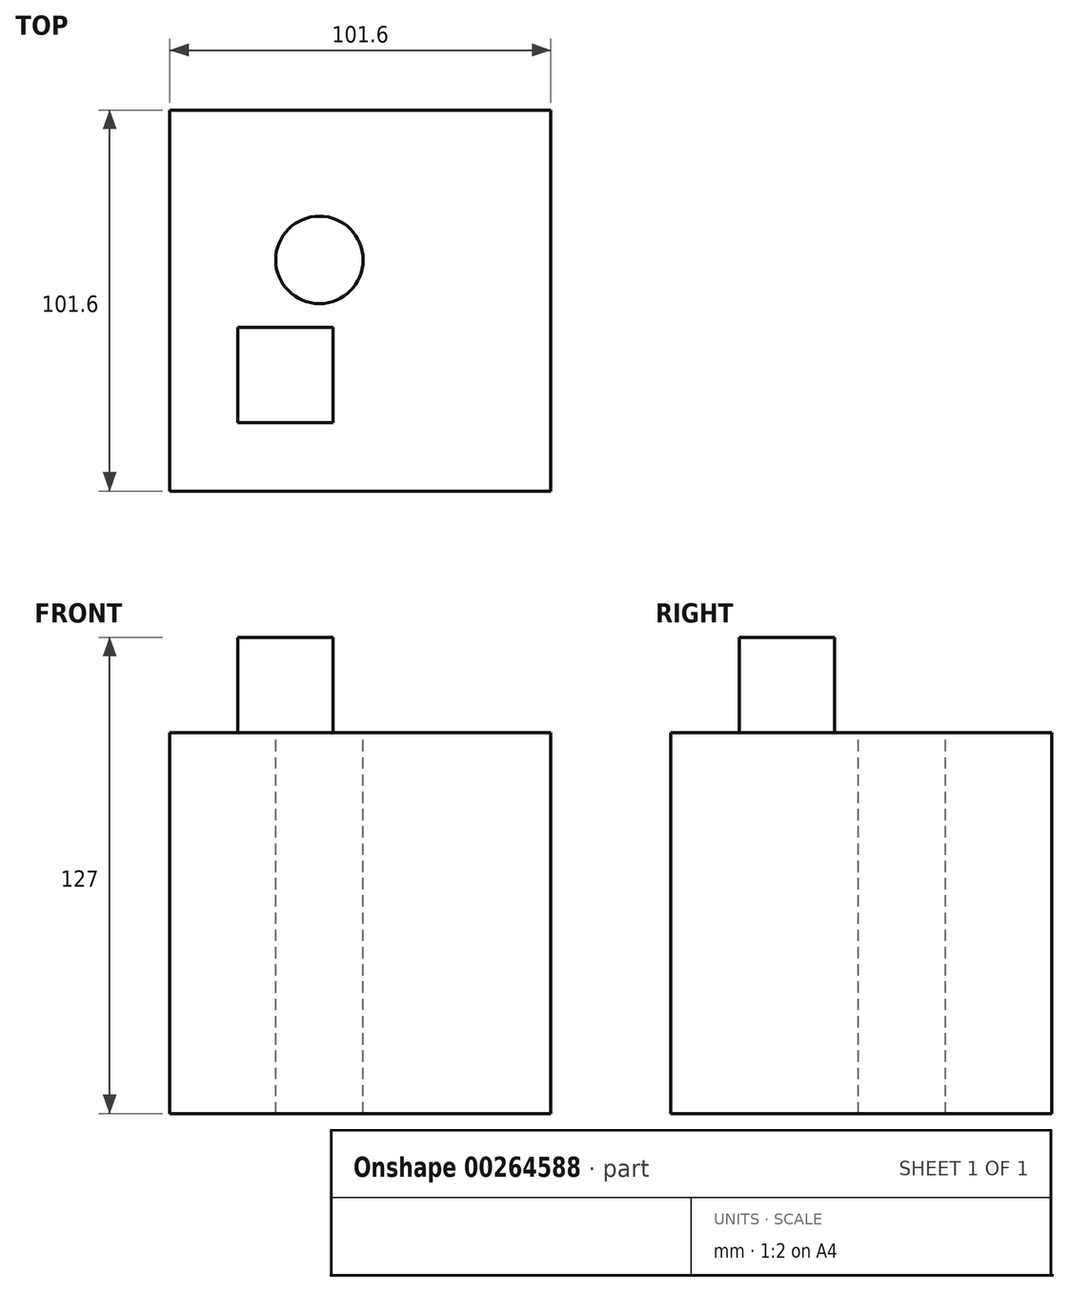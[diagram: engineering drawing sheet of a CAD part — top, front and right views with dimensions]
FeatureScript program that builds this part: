
annotation { "Feature Type Name" : "Feature", "Feature Type Description" : "" }
export const myFeature = defineFeature(function(context is Context, id is Id, definition is map)
    precondition{}
    {
        {
            var Q0;
            Q0=qCreatedBy(makeId("Front.planeOp"),FACE);
            var sketch = newSketch(context, id + "F0", { "sketchPlane" : qUnion([Q0])});
            skLineSegment(sketch, "E0.bottom", {"start": v(0, 0) * mm, "end": v(-101.6, 0) * mm});
            skLineSegment(sketch, "E0.top", {"start": v(0, 101.6) * mm, "end": v(-101.6, 101.6) * mm});
            skLineSegment(sketch, "E0.left", {"start": v(0, 0) * mm, "end": v(0, 101.6) * mm});
            skLineSegment(sketch, "E0.right", {"start": v(-101.6, 0) * mm, "end": v(-101.6, 101.6) * mm});
            skSolve(sketch);
        }
        {
            var Q0;
            Q0 = qSketchRegion(id + "F0", true);
            extrude(context, id + "F1", {"entities" : qUnion([Q0]), "depth" : 101.6 * mm});
        }
        {
            var Q0;
            Q0=makeQuery(id+"F1.opExtrude","SWEPT_FACE",FACE,{"disambiguationData":[OSD([sQuery(id+"F0.wireOp",EDGE,"E0.top")])]});
            var sketch = newSketch(context, id + "F2", { "sketchPlane" : qUnion([Q0])});
            skCircle(sketch, "E1", {"center": v(-61.7, -39.98) * mm, "radius": 11.65 * mm});
            skSolve(sketch);
        }
        {
            var Q0;
            Q0 = qSketchRegion(id + "F2", true);
            extrude(context, id + "F3", {"entities" : qUnion([Q0]), "operationType" : NewBodyOperationType.REMOVE, "oppositeDirection" : true, "depth" : 101.6 * mm});
        }
        {
            var Q0;
            Q0=makeQuery(id+"F1.opExtrude","SWEPT_FACE",FACE,{"disambiguationData":[OSD([sQuery(id+"F0.wireOp",EDGE,"E0.top")])]});
            var sketch = newSketch(context, id + "F4", { "sketchPlane" : qUnion([Q0])});
            skLineSegment(sketch, "E2.bottom", {"start": v(-83.5, -57.96) * mm, "end": v(-58.1, -57.96) * mm});
            skLineSegment(sketch, "E2.top", {"start": v(-83.5, -83.36) * mm, "end": v(-58.1, -83.36) * mm});
            skLineSegment(sketch, "E2.left", {"start": v(-83.5, -57.96) * mm, "end": v(-83.5, -83.36) * mm});
            skLineSegment(sketch, "E2.right", {"start": v(-58.1, -57.96) * mm, "end": v(-58.1, -83.36) * mm});
            skSolve(sketch);
        }
        {
            var Q0;
            Q0 = qSketchRegion(id + "F4", true);
            extrude(context, id + "F5", {"entities" : qUnion([Q0]), "operationType" : NewBodyOperationType.ADD, "depth" : 25.4 * mm});
        }
    });
